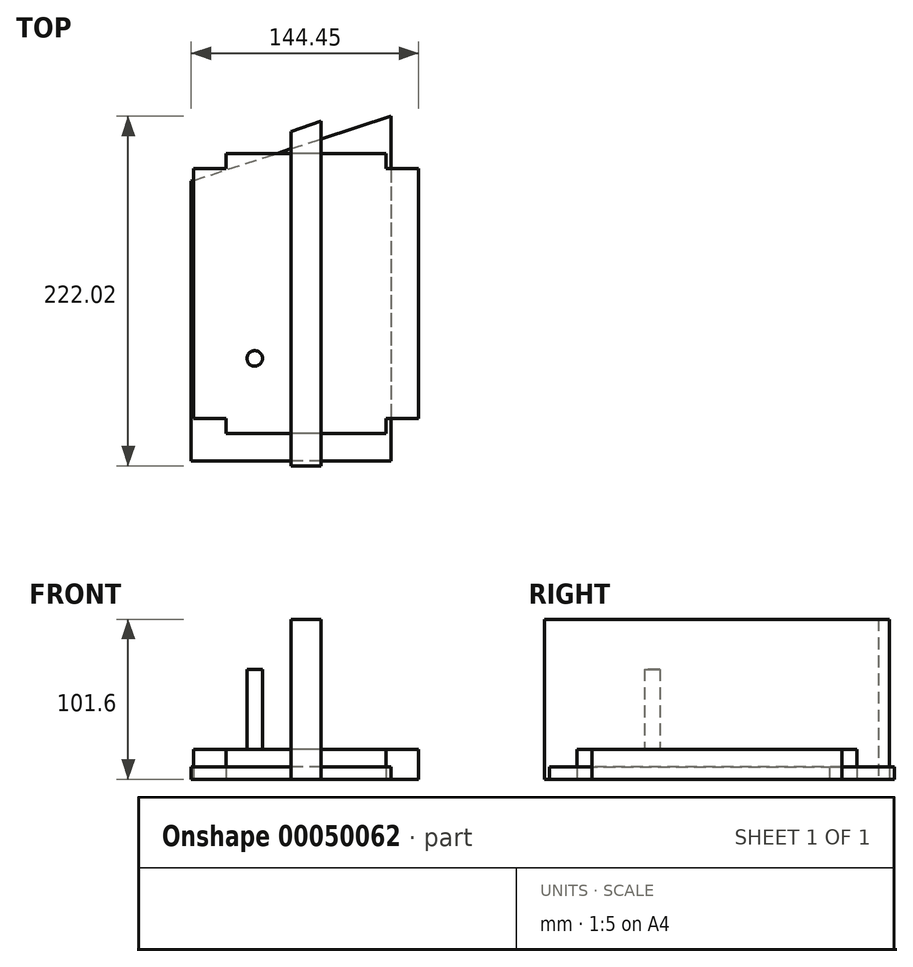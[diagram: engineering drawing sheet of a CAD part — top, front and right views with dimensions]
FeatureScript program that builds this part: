
annotation { "Feature Type Name" : "Feature", "Feature Type Description" : "" }
export const myFeature = defineFeature(function(context is Context, id is Id, definition is map)
    precondition{}
    {
        {
            var Q0;
            Q0=qCreatedBy(makeId("Top.planeOp"),FACE);
            var sketch = newSketch(context, id + "F0", { "sketchPlane" : qUnion([Q0])});
            skLineSegment(sketch, "E0", {"start": v(-73, -106.6) * mm, "end": v(-73, 71.2) * mm});
            skLineSegment(sketch, "E1", {"start": v(-73, 71.2) * mm, "end": v(54, 112.48) * mm});
            skLineSegment(sketch, "E2", {"start": v(54, 112.48) * mm, "end": v(54, -106.6) * mm});
            skLineSegment(sketch, "E3", {"start": v(54, -106.6) * mm, "end": v(-73, -106.6) * mm});
            skSolve(sketch);
        }
        {
            var Q0;
            Q0 = qSketchRegion(id + "F0", true);
            extrude(context, id + "F1", {"entities" : qUnion([Q0]), "depth" : 7.94 * mm});
        }
        {
            var Q0;
            Q0=makeQuery(id+"F1.opExtrude","SWEPT_BODY",BODY,{"disambiguationData":[OSD([sQuery(id+"F0.wireOp",EDGE,"E0"),sQuery(id+"F0.wireOp",EDGE,"E1"),sQuery(id+"F0.wireOp",EDGE,"E2"),sQuery(id+"F0.wireOp",EDGE,"E3")])]});
            transform(context, id + "F2", {"entities" : qUnion([Q0]), "transformType" : TransformType.TRANSLATION_3D, "dx" : 0 * mm, "dy" : 0 * mm, "dz" : 0 * mm, "makeCopy" : true});
        }
        {
            var Q0;
            Q0=qCreatedBy(makeId("Top.planeOp"),FACE);
            var sketch = newSketch(context, id + "F3", { "sketchPlane" : qUnion([Q0])});
            skLineSegment(sketch, "E4.rect.bottom", {"start": v(50.8, 44.45) * mm, "end": v(-50.8, 44.45) * mm});
            skLineSegment(sketch, "E4.rect.top", {"start": v(50.8, -44.45) * mm, "end": v(-50.8, -44.45) * mm});
            skLineSegment(sketch, "E4.rect.left", {"start": v(50.8, 44.45) * mm, "end": v(50.8, -44.45) * mm});
            skLineSegment(sketch, "E4.rect.right", {"start": v(-50.8, 44.45) * mm, "end": v(-50.8, -44.45) * mm});
            skPoint(sketch, "E4.rect.middle", {"position": v(0, 0) * mm});
            skSolve(sketch);
        }
        {
            var Q0;
            Q0=makeQuery(id+"F3.imprint","IMPRINT",FACE,{"disambiguationData":[TD([[makeQuery(id+"F3.imprint","IMPRINT",EDGE,{"derivedFrom":sQuery(id+"F3.wireOp",EDGE,"E4.rect.bottom")}),1.0]])]});
            extrude(context, id + "F4", {"entities" : qUnion([Q0]), "depth" : 19.05 * mm});
        }
        {
            var Q0;
            Q0=qCreatedBy(makeId("Top.planeOp"),FACE);
            var sketch = newSketch(context, id + "F5", { "sketchPlane" : qUnion([Q0])});
            skLineSegment(sketch, "E5.rect.top", {"start": v(-9.53, -109.54) * mm, "end": v(9.52, -109.54) * mm});
            skLineSegment(sketch, "E5.rect.left", {"start": v(-9.52, 102.6) * mm, "end": v(-9.53, -109.54) * mm});
            skLineSegment(sketch, "E5.rect.right", {"start": v(9.53, 109.54) * mm, "end": v(9.52, -109.54) * mm});
            skPoint(sketch, "E5.rect.middle", {"position": v(0, 0) * mm});
            skLineSegment(sketch, "E6", {"start": v(9.53, 109.54) * mm, "end": v(-9.52, 102.6) * mm});
            skSolve(sketch);
        }
        {
            var Q0;
            Q0=makeQuery(id+"F5.imprint","IMPRINT",FACE,{"disambiguationData":[TD([[makeQuery(id+"F5.imprint","IMPRINT",EDGE,{"derivedFrom":sQuery(id+"F5.wireOp",EDGE,"E5.rect.top")}),1.0]])]});
            extrude(context, id + "F6", {"entities" : qUnion([Q0]), "depth" : 101.6 * mm});
        }
        {
            var Q0;
            Q0=qCreatedBy(makeId("Top.planeOp"),FACE);
            var sketch = newSketch(context, id + "F7", { "sketchPlane" : qUnion([Q0])});
            skLineSegment(sketch, "E7.rect.bottom", {"start": v(71.44, 79.37) * mm, "end": v(-71.44, 79.37) * mm});
            skLineSegment(sketch, "E7.rect.top", {"start": v(71.44, -79.38) * mm, "end": v(-71.44, -79.38) * mm});
            skLineSegment(sketch, "E7.rect.left", {"start": v(71.44, 79.37) * mm, "end": v(71.44, -79.38) * mm});
            skLineSegment(sketch, "E7.rect.right", {"start": v(-71.44, 79.37) * mm, "end": v(-71.44, -79.38) * mm});
            skPoint(sketch, "E7.rect.middle", {"position": v(0, 0) * mm});
            skSolve(sketch);
        }
        {
            var Q0;
            Q0=makeQuery(id+"F7.imprint","IMPRINT",FACE,{"disambiguationData":[TD([[makeQuery(id+"F7.imprint","IMPRINT",EDGE,{"derivedFrom":sQuery(id+"F7.wireOp",EDGE,"E7.rect.bottom")}),1.0]])]});
            extrude(context, id + "F8", {"entities" : qUnion([Q0]), "depth" : 19.05 * mm});
        }
        {
            var Q0;
            Q0=qCreatedBy(makeId("Top.planeOp"),FACE);
            var sketch = newSketch(context, id + "F9", { "sketchPlane" : qUnion([Q0])});
            skLineSegment(sketch, "E8", {"start": v(-42.16, -36.02) * mm, "end": v(-39.96, 42.25) * mm});
            skLineSegment(sketch, "E9", {"start": v(-39.96, 42.25) * mm, "end": v(49.86, 57.65) * mm});
            skLineSegment(sketch, "E10", {"start": v(49.86, 57.65) * mm, "end": v(40.7, 31.07) * mm});
            skLineSegment(sketch, "E11", {"start": v(40.7, 31.07) * mm, "end": v(59.02, 14.39) * mm});
            skLineSegment(sketch, "E12", {"start": v(59.02, 14.39) * mm, "end": v(55.54, -21.9) * mm});
            skLineSegment(sketch, "E13", {"start": v(55.54, -21.9) * mm, "end": v(20.53, -29.97) * mm});
            skLineSegment(sketch, "E14", {"start": v(20.53, -29.97) * mm, "end": v(9.9, 17.5) * mm});
            skLineSegment(sketch, "E15", {"start": v(9.9, 17.5) * mm, "end": v(-19.06, 3.57) * mm});
            skLineSegment(sketch, "E16", {"start": v(-19.06, 3.57) * mm, "end": v(-18.88, -39.13) * mm});
            skLineSegment(sketch, "E17", {"start": v(-18.88, -39.13) * mm, "end": v(-42.16, -36.02) * mm});
            skSolve(sketch);
        }
        {
            var Q0;
            Q0=makeQuery(id+"F9.imprint","IMPRINT",FACE,{"disambiguationData":[TD([[makeQuery(id+"F9.imprint","IMPRINT",EDGE,{"derivedFrom":sQuery(id+"F9.wireOp",EDGE,"E8")}),-1.0]])]});
            extrude(context, id + "F10", {"entities" : qUnion([Q0]), "depth" : 25.4 * mm});
        }
        {
            var Q0;
            Q0=makeQuery(id+"F10.opExtrude","CAP_EDGE",EDGE,{"disambiguationData":[OSD([sQuery(id+"F9.wireOp",EDGE,"E16")])],"isStart":false});
            var Q1;
            Q1=makeQuery(id+"F10.opExtrude","CAP_EDGE",EDGE,{"disambiguationData":[OSD([sQuery(id+"F9.wireOp",EDGE,"E15")])],"isStart":false});
            var Q2;
            Q2=makeQuery(id+"F10.opExtrude","CAP_EDGE",EDGE,{"disambiguationData":[OSD([sQuery(id+"F9.wireOp",EDGE,"E14")])],"isStart":false});
            var Q3;
            Q3=makeQuery(id+"F10.opExtrude","CAP_FACE",FACE,{"disambiguationData":[OSD([sQuery(id+"F9.wireOp",EDGE,"E8"),sQuery(id+"F9.wireOp",EDGE,"E9"),sQuery(id+"F9.wireOp",EDGE,"E10"),sQuery(id+"F9.wireOp",EDGE,"E11"),sQuery(id+"F9.wireOp",EDGE,"E12"),sQuery(id+"F9.wireOp",EDGE,"E13"),sQuery(id+"F9.wireOp",EDGE,"E14"),sQuery(id+"F9.wireOp",EDGE,"E15"),sQuery(id+"F9.wireOp",EDGE,"E16"),sQuery(id+"F9.wireOp",EDGE,"E17")])],"isStart":false});
            fillet(context, id + "F11", {"entities" : qUnion([Q0, Q1, Q2, Q3]), "radius" : 5.08 * mm, "tangentPropagation" : true, "allowEdgeOverflow" : false});
        }
        {
            var Q0;
            Q0=makeQuery(id+"F10.opExtrude","SWEPT_BODY",BODY,{"disambiguationData":[OSD([sQuery(id+"F9.wireOp",EDGE,"E8"),sQuery(id+"F9.wireOp",EDGE,"E9"),sQuery(id+"F9.wireOp",EDGE,"E10"),sQuery(id+"F9.wireOp",EDGE,"E11"),sQuery(id+"F9.wireOp",EDGE,"E12"),sQuery(id+"F9.wireOp",EDGE,"E13"),sQuery(id+"F9.wireOp",EDGE,"E14"),sQuery(id+"F9.wireOp",EDGE,"E15"),sQuery(id+"F9.wireOp",EDGE,"E16"),sQuery(id+"F9.wireOp",EDGE,"E17")])]});
            deleteBodies(context, id + "F12", {"entities" : qUnion([Q0])});
        }
        {
            var Q0;
            Q0=qCreatedBy(makeId("Top.planeOp"),FACE);
            var sketch = newSketch(context, id + "F13", { "sketchPlane" : qUnion([Q0])});
            skLineSegment(sketch, "E18.rect.bottom", {"start": v(50.8, 88.9) * mm, "end": v(-50.8, 88.9) * mm});
            skLineSegment(sketch, "E18.rect.top", {"start": v(50.8, -88.9) * mm, "end": v(-50.8, -88.9) * mm});
            skLineSegment(sketch, "E18.rect.left", {"start": v(50.8, 88.9) * mm, "end": v(50.8, -88.9) * mm});
            skLineSegment(sketch, "E18.rect.right", {"start": v(-50.8, 88.9) * mm, "end": v(-50.8, -88.9) * mm});
            skPoint(sketch, "E18.rect.middle", {"position": v(0, 0) * mm});
            skCircle(sketch, "E19", {"center": v(0, 38.1) * mm, "radius": 19.05 * mm});
            skSolve(sketch);
        }
        {
            var Q0;
            Q0=makeQuery(id+"F13.imprint","IMPRINT",FACE,{"disambiguationData":[TD([[makeQuery(id+"F13.imprint","IMPRINT",EDGE,{"derivedFrom":sQuery(id+"F13.wireOp",EDGE,"E18.rect.bottom")}),1.0]])]});
            extrude(context, id + "F14", {"entities" : qUnion([Q0]), "depth" : 19.05 * mm});
        }
        {
            var Q0;
            Q0=makeQuery(id+"F14.opExtrude","CAP_FACE",FACE,{"disambiguationData":[OSD([sQuery(id+"F13.wireOp",EDGE,"E18.rect.bottom"),sQuery(id+"F13.wireOp",EDGE,"E18.rect.top"),sQuery(id+"F13.wireOp",EDGE,"E18.rect.left"),sQuery(id+"F13.wireOp",EDGE,"E18.rect.right"),sQuery(id+"F13.wireOp",EDGE,"E19")])],"isStart":false});
            var sketch = newSketch(context, id + "F15", { "sketchPlane" : qUnion([Q0])});
            skCircle(sketch, "E20", {"center": v(-32.69, -41.33) * mm, "radius": 4.92 * mm});
            skSolve(sketch);
        }
        {
            var Q0;
            Q0 = qSketchRegion(id + "F15", true);
            extrude(context, id + "F16", {"entities" : qUnion([Q0]), "operationType" : NewBodyOperationType.ADD, "depth" : 50.8 * mm});
        }
    });
